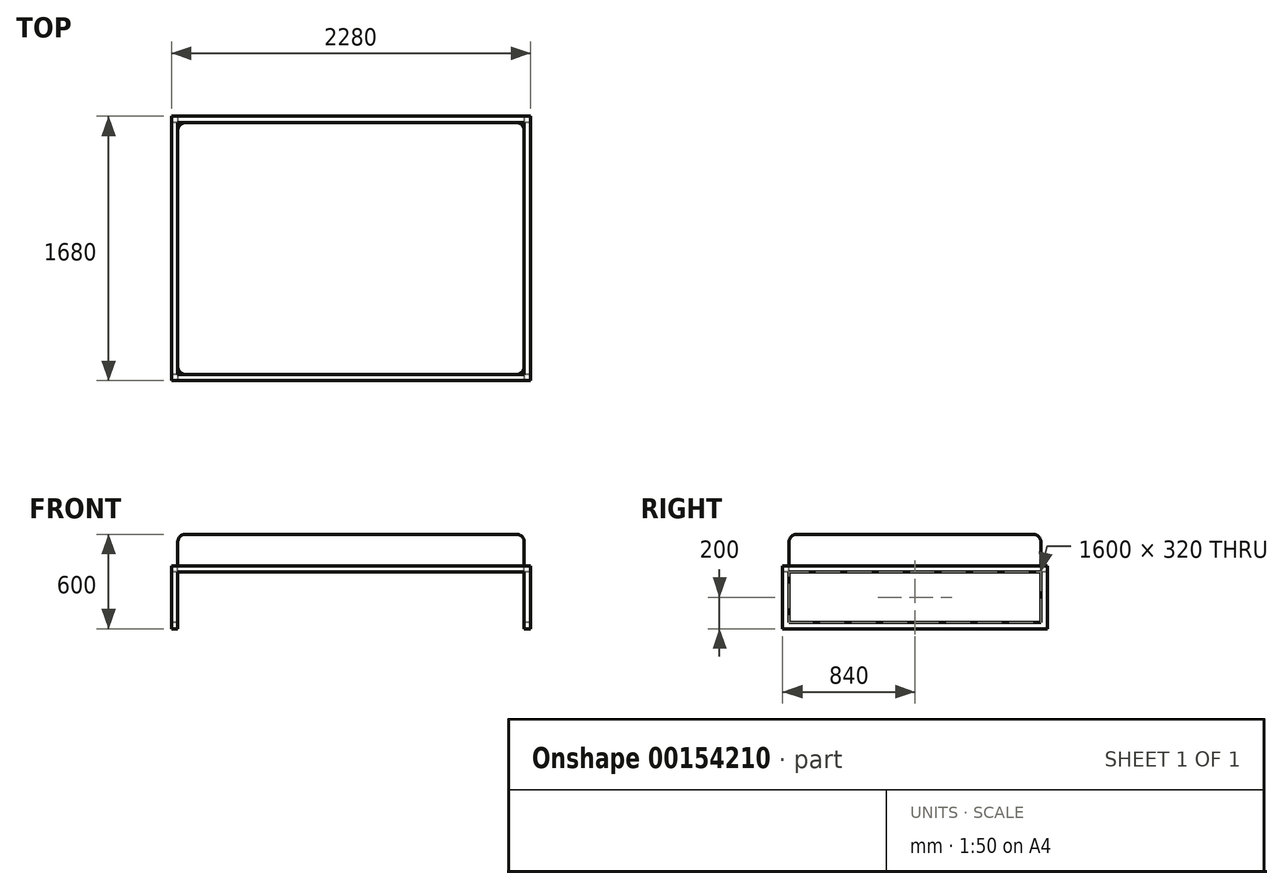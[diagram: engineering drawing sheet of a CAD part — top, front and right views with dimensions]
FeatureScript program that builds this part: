
annotation { "Feature Type Name" : "Feature", "Feature Type Description" : "" }
export const myFeature = defineFeature(function(context is Context, id is Id, definition is map)
    precondition{}
    {
        {
            var Q0;
            Q0=qCreatedBy(makeId("Top.planeOp"),FACE);
            var sketch = newSketch(context, id + "F0", { "sketchPlane" : qUnion([Q0])});
            skLineSegment(sketch, "E0.bottom", {"start": v(1100, 800) * mm, "end": v(-1100, 800) * mm});
            skLineSegment(sketch, "E0.top", {"start": v(1100, -800) * mm, "end": v(-1100, -800) * mm});
            skLineSegment(sketch, "E0.left", {"start": v(1100, 800) * mm, "end": v(1100, -800) * mm});
            skLineSegment(sketch, "E0.right", {"start": v(-1100, 800) * mm, "end": v(-1100, -800) * mm});
            skPoint(sketch, "E0.middle", {"position": v(0, 0) * mm});
            skLineSegment(sketch, "E1.bottom", {"start": v(1140, 840) * mm, "end": v(-1140, 840) * mm});
            skLineSegment(sketch, "E1.top", {"start": v(1140, -840) * mm, "end": v(-1140, -840) * mm});
            skLineSegment(sketch, "E1.left", {"start": v(1140, 840) * mm, "end": v(1140, -840) * mm});
            skLineSegment(sketch, "E1.right", {"start": v(-1140, 840) * mm, "end": v(-1140, -840) * mm});
            skSolve(sketch);
        }
        {
            var Q0;
            Q0=makeQuery(id+"F0.imprint","IMPRINT",FACE,{"disambiguationData":[TD([[makeQuery(id+"F0.imprint","IMPRINT",EDGE,{"derivedFrom":sQuery(id+"F0.wireOp",EDGE,"E0.bottom")}),-1.0]])]});
            extrude(context, id + "F1", {"entities" : qUnion([Q0]), "oppositeDirection" : true, "depth" : 400 * mm});
        }
        {
            var Q0;
            Q0=makeQuery(id+"F1.opExtrude","SWEPT_FACE",FACE,{"disambiguationData":[OSD([sQuery(id+"F0.wireOp",EDGE,"E1.top")])]});
            var sketch = newSketch(context, id + "F2", { "sketchPlane" : qUnion([Q0])});
            skLineSegment(sketch, "E2.bottom", {"start": v(-1100, -40) * mm, "end": v(1100, -40) * mm});
            skLineSegment(sketch, "E2.top", {"start": v(-1100, -400) * mm, "end": v(1100, -400) * mm});
            skLineSegment(sketch, "E2.left", {"start": v(-1100, -40) * mm, "end": v(-1100, -400) * mm});
            skLineSegment(sketch, "E2.right", {"start": v(1100, -40) * mm, "end": v(1100, -400) * mm});
            skSolve(sketch);
        }
        {
            var Q0;
            Q0=makeQuery(id+"F2.imprint","IMPRINT",FACE,{"disambiguationData":[TD([[makeQuery(id+"F2.imprint","IMPRINT",EDGE,{"derivedFrom":sQuery(id+"F2.wireOp",EDGE,"E2.bottom")}),-1.0]])]});
            extrude(context, id + "F3", {"entities" : qUnion([Q0]), "operationType" : NewBodyOperationType.REMOVE, "endBound" : BoundingType.THROUGH_ALL, "oppositeDirection" : true, "depth" : 25 * mm});
        }
        {
            var Q0;
            Q0=makeQuery(id+"F1.opExtrude","SWEPT_FACE",FACE,{"disambiguationData":[OSD([sQuery(id+"F0.wireOp",EDGE,"E1.right")])]});
            var sketch = newSketch(context, id + "F4", { "sketchPlane" : qUnion([Q0])});
            skLineSegment(sketch, "E3.bottom", {"start": v(-800, -40) * mm, "end": v(800, -40) * mm});
            skLineSegment(sketch, "E3.top", {"start": v(-800, -360) * mm, "end": v(800, -360) * mm});
            skLineSegment(sketch, "E3.left", {"start": v(-800, -40) * mm, "end": v(-800, -360) * mm});
            skLineSegment(sketch, "E3.right", {"start": v(800, -40) * mm, "end": v(800, -360) * mm});
            skSolve(sketch);
        }
        {
            var Q0;
            Q0=makeQuery(id+"F4.imprint","IMPRINT",FACE,{"disambiguationData":[TD([[makeQuery(id+"F4.imprint","IMPRINT",EDGE,{"derivedFrom":sQuery(id+"F4.wireOp",EDGE,"E3.bottom")}),-1.0]])]});
            extrude(context, id + "F5", {"entities" : qUnion([Q0]), "operationType" : NewBodyOperationType.REMOVE, "endBound" : BoundingType.THROUGH_ALL, "oppositeDirection" : true, "depth" : 25 * mm});
        }
        {
            var Q0;
            Q0=makeQuery(id+"F0.imprint","IMPRINT",FACE,{"disambiguationData":[TD([[makeQuery(id+"F0.imprint","IMPRINT",EDGE,{"derivedFrom":sQuery(id+"F0.wireOp",EDGE,"E0.bottom")}),1.0]])]});
            var Q1;
            Q1=sQuery(id+"F0.wireOp",EDGE,"E0.right");
            var Q2;
            Q2=sQuery(id+"F0.wireOp",EDGE,"E0.bottom");
            var Q3;
            Q3=sQuery(id+"F0.wireOp",EDGE,"E0.left");
            var Q4;
            Q4=sQuery(id+"F0.wireOp",EDGE,"E0.top");
            extrude(context, id + "F6", {"entities" : qUnion([Q0]), "bodyType" : ToolBodyType.SURFACE, "surfaceEntities" : qUnion([Q1, Q2, Q3, Q4]), "oppositeDirection" : true, "depth" : 100 * mm});
        }
        {
            var Q0;
            Q0=makeQuery(id+"F0.imprint","IMPRINT",FACE,{"disambiguationData":[TD([[makeQuery(id+"F0.imprint","IMPRINT",EDGE,{"derivedFrom":sQuery(id+"F0.wireOp",EDGE,"E0.bottom")}),1.0]])]});
            extrude(context, id + "F7", {"entities" : qUnion([Q0]), "depth" : 200 * mm});
        }
        {
            var Q0;
            Q0=makeQuery(id+"F7.opExtrude","CAP_EDGE",EDGE,{"disambiguationData":[OSD([sQuery(id+"F0.wireOp",EDGE,"E0.right")])],"isStart":false});
            var Q1;
            Q1=makeQuery(id+"F7.opExtrude","CAP_EDGE",EDGE,{"disambiguationData":[OSD([sQuery(id+"F0.wireOp",EDGE,"E0.top")])],"isStart":false});
            var Q2;
            Q2=makeQuery(id+"F7.opExtrude","SWEPT_EDGE",EDGE,{"disambiguationData":[OSD([sQuery(id+"F0.wireOp",EDGE,"E0.top"),sQuery(id+"F0.wireOp",EDGE,"E0.right")])]});
            var Q3;
            Q3=makeQuery(id+"F7.opExtrude","SWEPT_EDGE",EDGE,{"disambiguationData":[OSD([sQuery(id+"F0.wireOp",EDGE,"E0.top"),sQuery(id+"F0.wireOp",EDGE,"E0.left")])]});
            var Q4;
            Q4=makeQuery(id+"F7.opExtrude","CAP_EDGE",EDGE,{"disambiguationData":[OSD([sQuery(id+"F0.wireOp",EDGE,"E0.left")])],"isStart":false});
            var Q5;
            Q5=makeQuery(id+"F7.opExtrude","CAP_EDGE",EDGE,{"disambiguationData":[OSD([sQuery(id+"F0.wireOp",EDGE,"E0.bottom")])],"isStart":false});
            var Q6;
            Q6=makeQuery(id+"F7.opExtrude","SWEPT_EDGE",EDGE,{"disambiguationData":[OSD([sQuery(id+"F0.wireOp",EDGE,"E0.bottom"),sQuery(id+"F0.wireOp",EDGE,"E0.left")])]});
            var Q7;
            Q7=makeQuery(id+"F7.opExtrude","SWEPT_EDGE",EDGE,{"disambiguationData":[OSD([sQuery(id+"F0.wireOp",EDGE,"E0.bottom"),sQuery(id+"F0.wireOp",EDGE,"E0.right")])]});
            fillet(context, id + "F8", {"entities" : qUnion([Q0, Q1, Q2, Q3, Q4, Q5, Q6, Q7]), "radius" : 50 * mm, "tangentPropagation" : true, "allowEdgeOverflow" : false});
        }
    });
